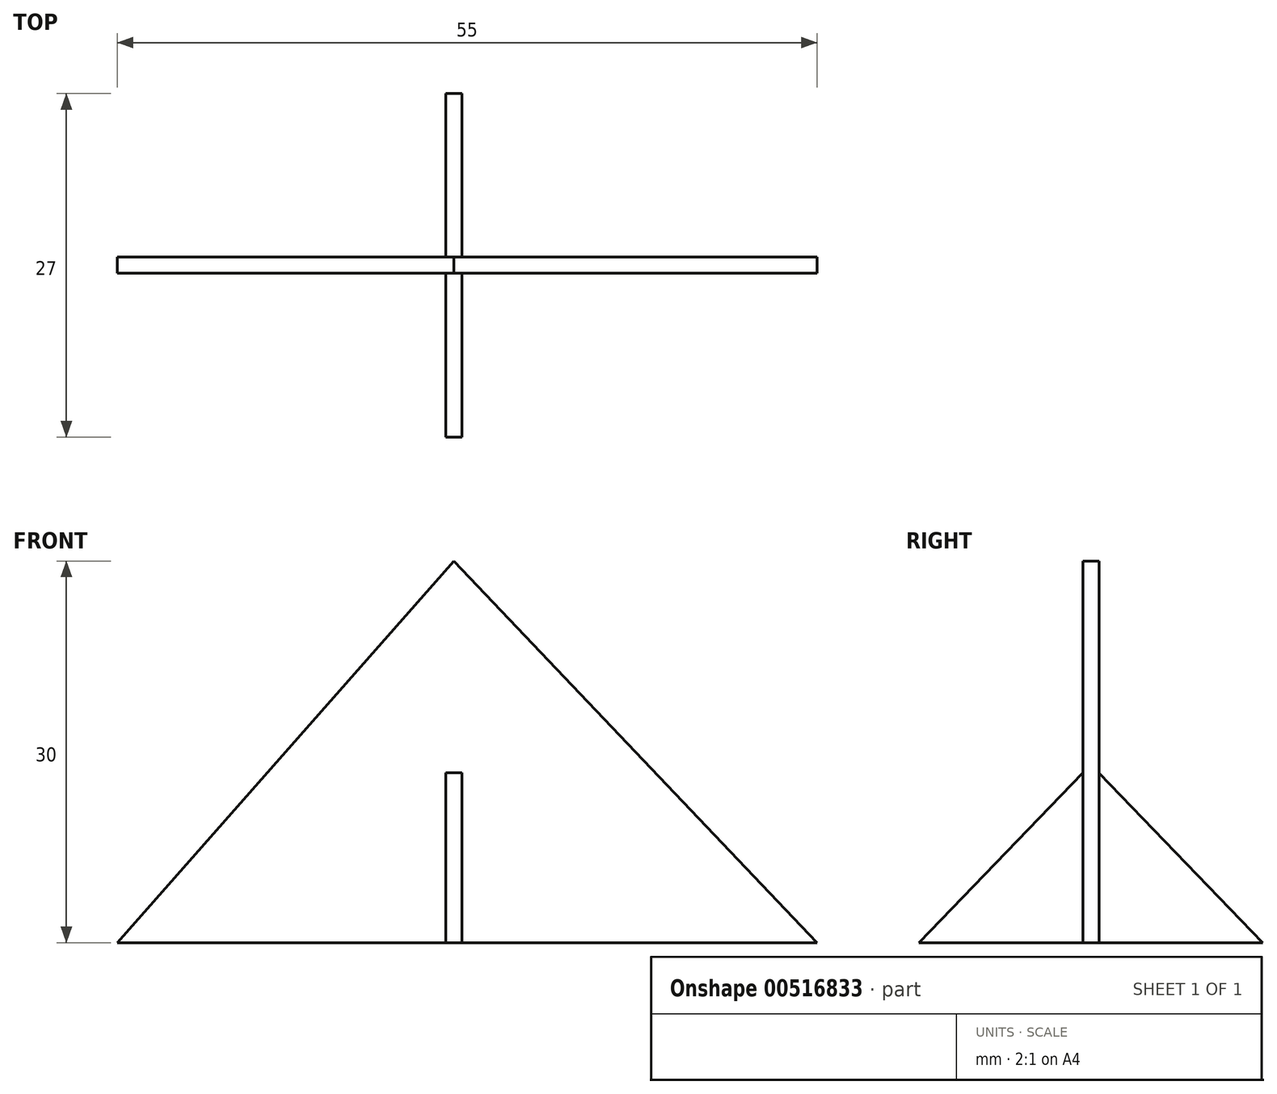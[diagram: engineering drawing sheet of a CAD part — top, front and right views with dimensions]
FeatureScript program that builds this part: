
annotation { "Feature Type Name" : "Feature", "Feature Type Description" : "" }
export const myFeature = defineFeature(function(context is Context, id is Id, definition is map)
    precondition{}
    {
        {
            var Q0;
            Q0=qCreatedBy(makeId("Front.planeOp"),FACE);
            var sketch = newSketch(context, id + "F0", { "sketchPlane" : qUnion([Q0])});
            skLineSegment(sketch, "E0", {"start": v(-26.46, 0) * mm, "end": v(28.54, 0) * mm});
            skLineSegment(sketch, "E1", {"start": v(0, 30) * mm, "end": v(-26.46, 0) * mm});
            skLineSegment(sketch, "E2", {"start": v(0, 30) * mm, "end": v(28.54, 0) * mm});
            skSolve(sketch);
        }
        {
            var Q0;
            Q0=makeQuery(id+"F0.imprint","IMPRINT",FACE,{"disambiguationData":[TD([[makeQuery(id+"F0.imprint","IMPRINT",EDGE,{"derivedFrom":sQuery(id+"F0.wireOp",EDGE,"E0")}),1.0]])]});
            extrude(context, id + "F1", {"entities" : qUnion([Q0]), "endBound" : BoundingType.SYMMETRIC, "depth" : 1.27 * mm, "offsetDistance" : 25.4 * mm});
        }
        {
            var Q0;
            Q0=qCreatedBy(makeId("Right.planeOp"),FACE);
            var sketch = newSketch(context, id + "F2", { "sketchPlane" : qUnion([Q0])});
            skLineSegment(sketch, "E3", {"start": v(13.48, 0) * mm, "end": v(-13.52, 0) * mm});
            skLineSegment(sketch, "E4", {"start": v(0, 0) * mm, "end": v(-0.02, 14) * mm});
            skPoint(sketch, "E4.endSnap0", {"position": v(-0.02, 0) * mm});
            skLineSegment(sketch, "E5", {"start": v(-0.02, 14) * mm, "end": v(13.48, 0) * mm});
            skLineSegment(sketch, "E6", {"start": v(-13.52, 0) * mm, "end": v(-0.02, 14) * mm});
            skSolve(sketch);
        }
        {
            var Q0;
            {var subQ2=sQuery(id+"F2.wireOp",EDGE,"E4");Q0=makeQuery(id+"F2.imprint","IMPRINT",FACE,{"disambiguationData":[TD([[makeQuery(id+"F2.imprint","IMPRINT",EDGE,{"derivedFrom":subQ2}),-1.0]])]});}
            var Q1;
            {var subQ2=sQuery(id+"F2.wireOp",EDGE,"E4");Q1=makeQuery(id+"F2.imprint","IMPRINT",FACE,{"disambiguationData":[TD([[makeQuery(id+"F2.imprint","IMPRINT",EDGE,{"derivedFrom":subQ2}),1.0]])]});}
            extrude(context, id + "F3", {"entities" : qUnion([Q0, Q1]), "operationType" : NewBodyOperationType.ADD, "endBound" : BoundingType.SYMMETRIC, "depth" : 1.27 * mm, "offsetDistance" : 25.4 * mm});
        }
    });
